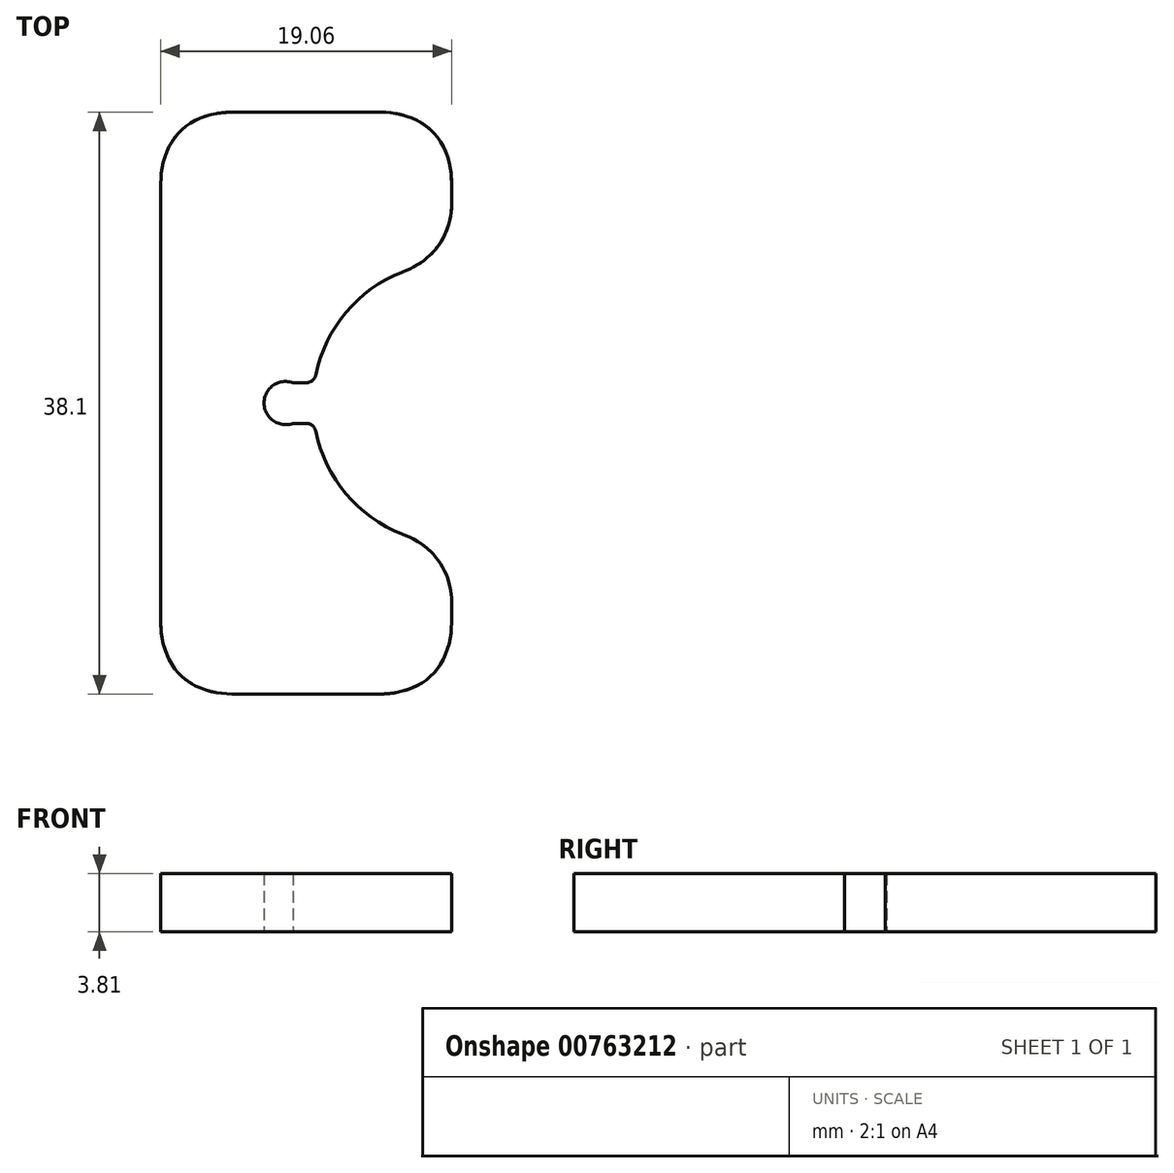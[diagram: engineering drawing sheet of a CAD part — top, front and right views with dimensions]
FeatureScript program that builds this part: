
annotation { "Feature Type Name" : "Feature", "Feature Type Description" : "" }
export const myFeature = defineFeature(function(context is Context, id is Id, definition is map)
    precondition{}
    {
        {
            var Q0;
            Q0=qCreatedBy(makeId("Top.planeOp"),FACE);
            var sketch = newSketch(context, id + "F0", { "sketchPlane" : qUnion([Q0])});
            skLineSegment(sketch, "E0.bottom", {"start": v(9.53, 19.05) * mm, "end": v(-9.53, 19.05) * mm});
            skLineSegment(sketch, "E0.top", {"start": v(9.52, -19.05) * mm, "end": v(-9.53, -19.05) * mm});
            skLineSegment(sketch, "E0.left", {"start": v(9.53, 19.05) * mm, "end": v(9.52, 9.22) * mm});
            skLineSegment(sketch, "E0.right", {"start": v(-9.53, 19.05) * mm, "end": v(-9.53, -19.05) * mm});
            skPoint(sketch, "E0.middle", {"position": v(0, 0) * mm});
            skArc(sketch, "E1", {"start": v(9.65, 9.22) * mm, "mid": v(3.82, 7.14) * mm, "end": v(0.62, 1.83) * mm});
            skArc(sketch, "E2", {"start": v(-0.86, 1.32) * mm, "mid": v(-2.76, 0) * mm, "end": v(-0.86, -1.33) * mm});
            skLineSegment(sketch, "E3", {"start": v(-0.86, -1.32) * mm, "end": v(0, -1.32) * mm});
            skLineSegment(sketch, "E4", {"start": v(-0.86, 1.32) * mm, "end": v(0, 1.32) * mm});
            skArc(sketch, "E5.trimOffspring", {"start": v(0.62, -1.83) * mm, "mid": v(3.82, -7.14) * mm, "end": v(9.65, -9.22) * mm});
            skPoint(sketch, "E6.visualSharp", {"position": v(0.53, -1.32) * mm});
            skArc(sketch, "E6.filletArc", {"start": v(0.62, -1.83) * mm, "mid": v(0.4, -1.47) * mm, "end": v(0, -1.32) * mm});
            skPoint(sketch, "E7.visualSharp", {"position": v(0.53, 1.32) * mm});
            skArc(sketch, "E7.filletArc", {"start": v(0, 1.33) * mm, "mid": v(0.4, 1.47) * mm, "end": v(0.62, 1.83) * mm});
            skLineSegment(sketch, "E8", {"start": v(-1.35, 0) * mm, "end": v(9.65, 0) * mm, "construction": true});
            skLineSegment(sketch, "E9", {"start": v(0, 1.32) * mm, "end": v(0, -1.32) * mm, "construction": true});
            skLineSegment(sketch, "E10.trimOffspring", {"start": v(9.52, -9.22) * mm, "end": v(9.52, -19.05) * mm});
            skSolve(sketch);
        }
        {
            var Q0;
            Q0=makeQuery(id+"F0.imprint","IMPRINT",FACE,{"disambiguationData":[TD([[makeQuery(id+"F0.imprint","IMPRINT",EDGE,{"derivedFrom":sQuery(id+"F0.wireOp",EDGE,"E0.bottom")}),1.0]])]});
            extrude(context, id + "F1", {"entities" : qUnion([Q0]), "depth" : 3.8 * mm, "offsetDistance" : 25.4 * mm});
        }
        {
            var Q0;
            Q0=makeQuery(id+"F1.opExtrude","SWEPT_EDGE",EDGE,{"disambiguationData":[OSD([sQuery(id+"F0.wireOp",EDGE,"E0.bottom"),sQuery(id+"F0.wireOp",EDGE,"E0.right")])]});
            var Q1;
            Q1=makeQuery(id+"F1.opExtrude","SWEPT_EDGE",EDGE,{"disambiguationData":[OSD([sQuery(id+"F0.wireOp",EDGE,"E0.bottom"),sQuery(id+"F0.wireOp",EDGE,"E0.left")])]});
            var Q2;
            Q2=makeQuery(id+"F1.opExtrude","SWEPT_EDGE",EDGE,{"disambiguationData":[OSD([sQuery(id+"F0.wireOp",EDGE,"E0.left"),sQuery(id+"F0.wireOp",EDGE,"E1")])]});
            var Q3;
            Q3=makeQuery(id+"F1.opExtrude","SWEPT_EDGE",EDGE,{"disambiguationData":[OSD([sQuery(id+"F0.wireOp",EDGE,"E5.trimOffspring"),sQuery(id+"F0.wireOp",EDGE,"E10.trimOffspring")])]});
            var Q4;
            Q4=makeQuery(id+"F1.opExtrude","SWEPT_EDGE",EDGE,{"disambiguationData":[OSD([sQuery(id+"F0.wireOp",EDGE,"E0.top"),sQuery(id+"F0.wireOp",EDGE,"E10.trimOffspring")])]});
            var Q5;
            Q5=makeQuery(id+"F1.opExtrude","SWEPT_EDGE",EDGE,{"disambiguationData":[OSD([sQuery(id+"F0.wireOp",EDGE,"E0.top"),sQuery(id+"F0.wireOp",EDGE,"E0.right")])]});
            fillet(context, id + "F2", {"entities" : qUnion([Q0, Q1, Q2, Q3, Q4, Q5]), "tangentPropagation" : true, "crossSection" : FilletCrossSection.CURVATURE, "radius" : 5.08 * mm, "magnitude" : 0.5, "defaultsChanged" : false, "vertexSettings" : []});
        }
    });
